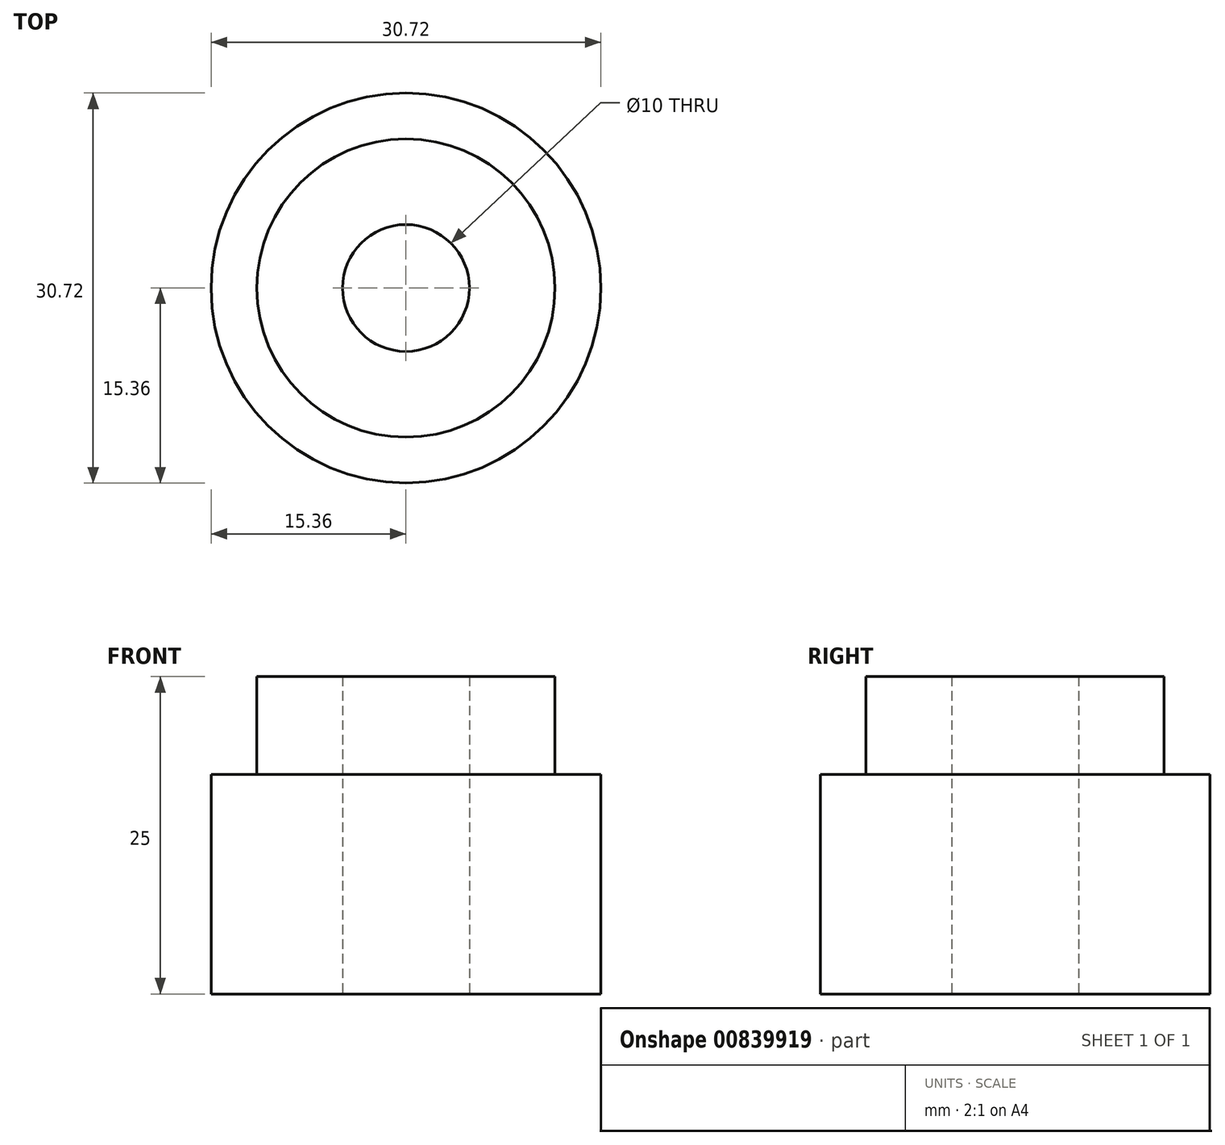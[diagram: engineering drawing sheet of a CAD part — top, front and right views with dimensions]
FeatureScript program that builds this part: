
annotation { "Feature Type Name" : "Feature", "Feature Type Description" : "" }
export const myFeature = defineFeature(function(context is Context, id is Id, definition is map)
    precondition{}
    {
        {
            var Q0;
            Q0=qCreatedBy(makeId("Top.planeOp"),FACE);
            var sketch = newSketch(context, id + "F0", { "sketchPlane" : qUnion([Q0])});
            skCircle(sketch, "E0", {"center": v(0, 0) * mm, "radius": 5 * mm});
            skCircle(sketch, "E1", {"center": v(0, 0) * mm, "radius": 15.36 * mm});
            skSolve(sketch);
        }
        {
            var Q0;
            Q0=qSketchRegion(id+"F0",true);
            extrude(context, id + "F1", {"entities" : qUnion([Q0]), "depth" : 25 * mm, "offsetDistance" : 25 * mm});
        }
        {
            var Q0;
            Q0=makeQuery(id+"F1.opExtrude","CAP_FACE",FACE,{"disambiguationData":[OSD([sQuery(id+"F0.wireOp",EDGE,"E0"),sQuery(id+"F0.wireOp",EDGE,"E1")])],"isStart":false});
            var sketch = newSketch(context, id + "F2", { "sketchPlane" : qUnion([Q0])});
            skCircle(sketch, "E2", {"center": v(0, 0) * mm, "radius": 11.75 * mm});
            skSolve(sketch);
        }
        {
            var Q0;
            Q0=makeQuery(id+"F2.imprint","IMPRINT",FACE,{"disambiguationData":[TD([[makeQuery(id+"F2.imprint","IMPRINT",EDGE,{"derivedFrom":sQuery(id+"F2.wireOp",EDGE,"E2")}),-1.0]])]});
            extrude(context, id + "F3", {"entities" : qUnion([Q0]), "operationType" : NewBodyOperationType.REMOVE, "oppositeDirection" : true, "depth" : 7.7 * mm, "offsetDistance" : 25 * mm});
        }
    });
